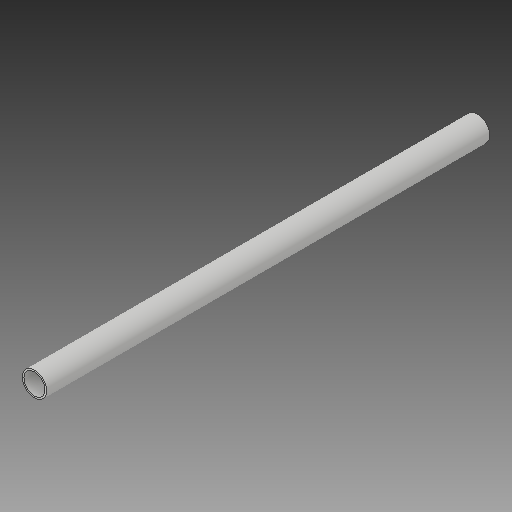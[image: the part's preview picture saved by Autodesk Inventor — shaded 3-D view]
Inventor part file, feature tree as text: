
AUTODESK INVENTOR PART (.ipt)
format: ipt  version: 2018.3 (Build 223284000, 284)  size: 82,432 bytes
history: native  units: mm
features: other x1, extrude x1, sketch x1
ambient origin geometry x8: Origin, YZ Plane, XZ Plane, XY Plane, X Axis, Y Axis, Z Axis, Center Point
bodies: Body1 (feature_tree)
feature tree (3):
  other  "ソリッド1"
  extrude  "押し出し1"  Depth=16.0mm
  sketch  "スケッチ1"
